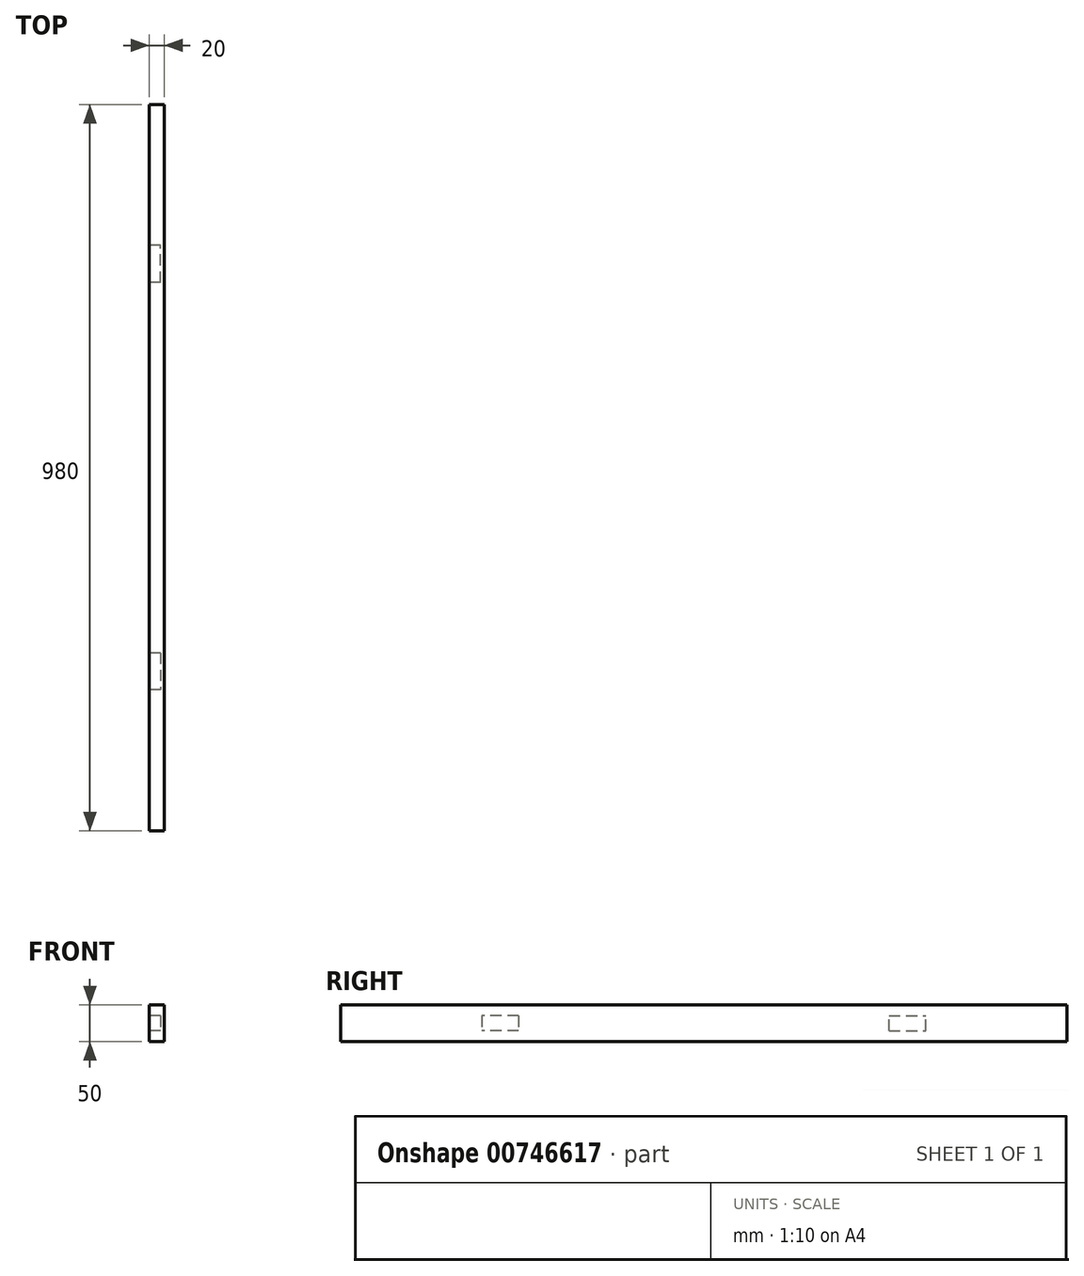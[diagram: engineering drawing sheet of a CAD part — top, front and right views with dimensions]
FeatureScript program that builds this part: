
annotation { "Feature Type Name" : "Feature", "Feature Type Description" : "" }
export const myFeature = defineFeature(function(context is Context, id is Id, definition is map)
    precondition{}
    {
        {
            var Q0;
            Q0=qCreatedBy(makeId("Front.planeOp"),FACE);
            var sketch = newSketch(context, id + "F0", { "sketchPlane" : qUnion([Q0])});
            skLineSegment(sketch, "E0.bottom", {"start": v(10, -25) * mm, "end": v(-10, -25) * mm});
            skLineSegment(sketch, "E0.top", {"start": v(10, 25) * mm, "end": v(-10, 25) * mm});
            skLineSegment(sketch, "E0.left", {"start": v(10, -25) * mm, "end": v(10, 25) * mm});
            skLineSegment(sketch, "E0.right", {"start": v(-10, -25) * mm, "end": v(-10, 25) * mm});
            skPoint(sketch, "E0.middle", {"position": v(0, 0) * mm});
            skSolve(sketch);
        }
        {
            var Q0;
            Q0=makeQuery(id+"F0.imprint","IMPRINT",FACE,{"disambiguationData":[TD([[makeQuery(id+"F0.imprint","IMPRINT",EDGE,{"derivedFrom":sQuery(id+"F0.wireOp",EDGE,"E0.bottom")}),-1.0]])]});
            extrude(context, id + "F1", {"entities" : qUnion([Q0]), "oppositeDirection" : true, "depth" : 980 * mm, "offsetDistance" : 25 * mm});
        }
        {
            var Q0;
            Q0=makeQuery(id+"F1.opExtrude","SWEPT_FACE",FACE,{"disambiguationData":[OSD([sQuery(id+"F0.wireOp",EDGE,"E0.right")])]});
            var sketch = newSketch(context, id + "F2", { "sketchPlane" : qUnion([Q0])});
            skLineSegment(sketch, "E1.bottom", {"start": v(-740, -10) * mm, "end": v(-790, -10) * mm});
            skLineSegment(sketch, "E1.top", {"start": v(-740, 10) * mm, "end": v(-790, 10) * mm});
            skLineSegment(sketch, "E1.left", {"start": v(-740, -10) * mm, "end": v(-740, 10) * mm});
            skLineSegment(sketch, "E1.right", {"start": v(-790, -10) * mm, "end": v(-790, 10) * mm});
            skPoint(sketch, "E1.middle", {"position": v(-765, 0) * mm});
            skLineSegment(sketch, "E2.bottom", {"start": v(-240, 10) * mm, "end": v(-190, 10) * mm});
            skLineSegment(sketch, "E2.top", {"start": v(-240, -10) * mm, "end": v(-190, -10) * mm});
            skLineSegment(sketch, "E2.left", {"start": v(-240, 10) * mm, "end": v(-240, -10) * mm});
            skLineSegment(sketch, "E2.right", {"start": v(-190, 10) * mm, "end": v(-190, -10) * mm});
            skPoint(sketch, "E2.middle", {"position": v(-215, 0) * mm});
            skSolve(sketch);
        }
        {
            var Q0;
            Q0=qSketchRegion(id+"F2",true);
            extrude(context, id + "F3", {"entities" : qUnion([Q0]), "operationType" : NewBodyOperationType.REMOVE, "oppositeDirection" : true, "depth" : 15 * mm, "offsetDistance" : 25 * mm});
        }
    });
